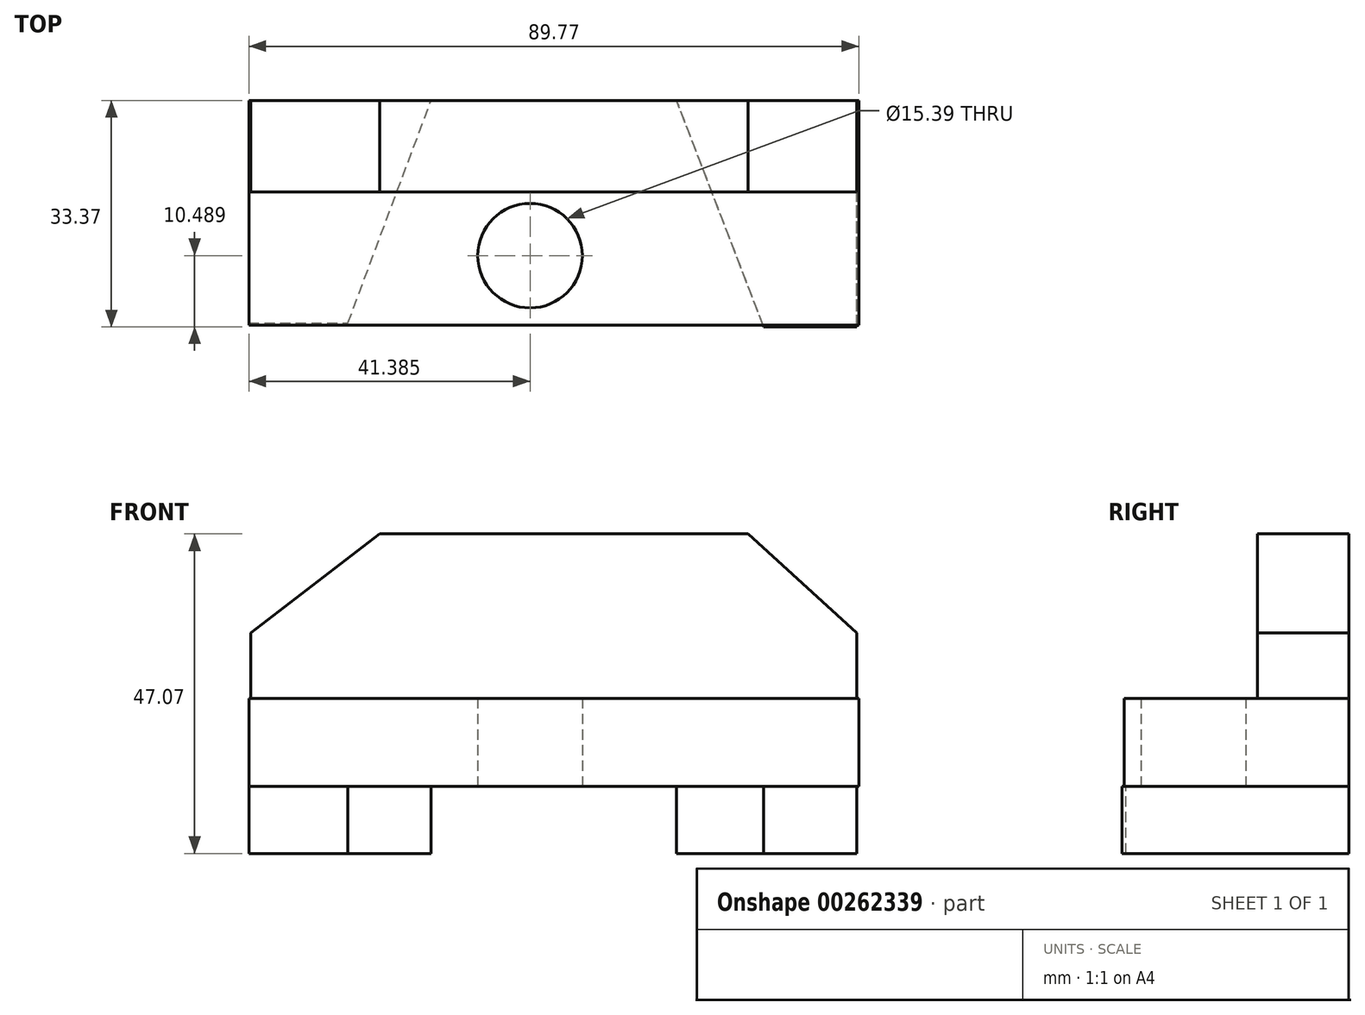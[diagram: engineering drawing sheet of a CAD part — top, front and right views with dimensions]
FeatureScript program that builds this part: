
annotation { "Feature Type Name" : "Feature", "Feature Type Description" : "" }
export const myFeature = defineFeature(function(context is Context, id is Id, definition is map)
    precondition{}
    {
        {
            var Q0;
            Q0=qCreatedBy(makeId("Front.planeOp"),FACE);
            var sketch = newSketch(context, id + "F0", { "sketchPlane" : qUnion([Q0])});
            skLineSegment(sketch, "E0", {"start": v(-46.05, 22.59) * mm, "end": v(-46.05, 0) * mm});
            skLineSegment(sketch, "E1", {"start": v(-46.05, 0) * mm, "end": v(43.14, 0) * mm});
            skLineSegment(sketch, "E2", {"start": v(43.14, 0) * mm, "end": v(43.14, 22.59) * mm});
            skLineSegment(sketch, "E3", {"start": v(43.14, 22.59) * mm, "end": v(27.1, 37.16) * mm});
            skLineSegment(sketch, "E4", {"start": v(27.1, 37.16) * mm, "end": v(-27.1, 37.16) * mm});
            skLineSegment(sketch, "E5", {"start": v(-27.1, 37.16) * mm, "end": v(-46.05, 22.59) * mm});
            skSolve(sketch);
        }
        {
            var Q0;
            Q0 = qSketchRegion(id + "F0", true);
            extrude(context, id + "F1", {"entities" : qUnion([Q0]), "depth" : 13.46 * mm});
        }
        {
            var Q0;
            Q0=qCreatedBy(makeId("Top.planeOp"),FACE);
            var sketch = newSketch(context, id + "F2", { "sketchPlane" : qUnion([Q0])});
            skLineSegment(sketch, "E6.bottom", {"start": v(-46.34, 0) * mm, "end": v(43.43, 0) * mm});
            skLineSegment(sketch, "E6.top", {"start": v(-46.34, -33.08) * mm, "end": v(43.43, -33.08) * mm});
            skLineSegment(sketch, "E6.left", {"start": v(-46.34, 0) * mm, "end": v(-46.34, -33.08) * mm});
            skLineSegment(sketch, "E6.right", {"start": v(43.43, 0) * mm, "end": v(43.43, -33.08) * mm});
            skSolve(sketch);
        }
        {
            var Q0;
            Q0 = qSketchRegion(id + "F2", true);
            extrude(context, id + "F3", {"entities" : qUnion([Q0]), "operationType" : NewBodyOperationType.ADD, "depth" : 12.95 * mm});
        }
        {
            var Q0;
            Q0=qCreatedBy(makeId("Top.planeOp"),FACE);
            var sketch = newSketch(context, id + "F4", { "sketchPlane" : qUnion([Q0])});
            skCircle(sketch, "E7", {"center": v(-4.96, -22.88) * mm, "radius": 7.7 * mm});
            skSolve(sketch);
        }
        {
            var Q0;
            Q0 = qSketchRegion(id + "F4", true);
            extrude(context, id + "F5", {"entities" : qUnion([Q0]), "operationType" : NewBodyOperationType.REMOVE, "depth" : 63.5 * mm});
        }
        {
            var Q0;
            Q0=qCreatedBy(makeId("Top.planeOp"),FACE);
            var sketch = newSketch(context, id + "F6", { "sketchPlane" : qUnion([Q0])});
            skLineSegment(sketch, "E8.bottom", {"start": v(-46.34, -32.8) * mm, "end": v(-31.77, -32.8) * mm});
            skLineSegment(sketch, "E8.top", {"start": v(-46.34, 0) * mm, "end": v(-31.77, 0) * mm});
            skLineSegment(sketch, "E8.left", {"start": v(-46.34, -32.8) * mm, "end": v(-46.34, 0) * mm});
            skLineSegment(sketch, "E8.right", {"start": v(-31.77, -32.8) * mm, "end": v(-31.77, 0) * mm});
            skLineSegment(sketch, "E9", {"start": v(-31.77, -32.8) * mm, "end": v(-19.53, 0) * mm});
            skLineSegment(sketch, "E10", {"start": v(-19.53, 0) * mm, "end": v(-31.77, 0) * mm});
            skLineSegment(sketch, "E11.bottom", {"start": v(43.14, -33.37) * mm, "end": v(29.44, -33.37) * mm});
            skLineSegment(sketch, "E11.top", {"start": v(43.14, 0) * mm, "end": v(29.44, 0) * mm});
            skLineSegment(sketch, "E11.left", {"start": v(43.14, -33.37) * mm, "end": v(43.14, 0) * mm});
            skLineSegment(sketch, "E11.right", {"start": v(29.44, -33.37) * mm, "end": v(29.44, 0) * mm});
            skLineSegment(sketch, "E12", {"start": v(29.44, -33.37) * mm, "end": v(16.61, 0) * mm});
            skLineSegment(sketch, "E13", {"start": v(16.61, 0) * mm, "end": v(29.44, 0) * mm});
            skSolve(sketch);
        }
        {
            var Q0;
            Q0 = qSketchRegion(id + "F6", true);
            extrude(context, id + "F7", {"entities" : qUnion([Q0]), "operationType" : NewBodyOperationType.ADD, "oppositeDirection" : true, "depth" : 9.9 * mm});
        }
    });
